# Revit family: PGR_Noken_SntryApplncTrps_Rondo
name_source: partatom
category: Plumbing Fixtures
revit_build: Autodesk Revit 2017 (Build: 20171027_0315(x64)
units: mm (PartAtom-declared; Revit-internal decimal feet)

## family parameters
Always vertical = Yes
Cut with Voids When Loaded = No
Host = Wall
OmniClass Number = 23.45.55.11
OmniClass Title = Sanitary Components
Part Type = Normal
Room Calculation Point = No
Round Connector Dimension = Use Diameter
Shared = Yes

## types (1)
- Rondo-100067431
    AccessibilityPerformance = SeeProductInformation for technical PDF
    ApplicationType = Basin
    AssetType = Fixed
    BIMObjectName = PGR_Noken_SanitaryApplianceTraps_Rondo_Chrome-65x330-380x145-255mm-100067431
    Category = Pr_65_52_25_75: Sanitary appliance traps
    CodePerformance = EN 274
    Collection = Rondo
    Color = Chrome
    Description = Rondo Bottle trap. UK size 35 mm diameter. Material brass, finish chrome plated, nominal length 330-380 mm, nominal width 65 mm, nominal height 145-255 mm, net product weight 0,9 kg . Normative UNE EN 274
    DurationUnit = year
    Features = See ProductInformation for technical PDF
    Finish = Chrome plated
    IfcExportAs = IfcWasteTerminalType
    IfcExportType = WasteTrap
    InletConnectionSize = 40 mm  [stored 0.131234 ft]
    ManufacturerURL = www.noken.com
    Material = Brass
    MaterialMetal = PGR_Noken_Brass_Chrome
    Model = 100067431
    ModelNumber = 100067431
    ModelReference = RONDO BOTTLE TRAP
    NBSDescription = Sanitary appliance traps
    NBSReference = 90-10-60/410
    Name = SanitaryApplianceTraps_Rondo_Chrome-65x330-380x145-255mm-100067431
    NettWeight = 0.9
    NominalHeight = 255 mm  [stored 0.836614 ft]
    NominalHeightRange = 145-255
    NominalLength = 380 mm
    NominalLengthRange = 330-380
    NominalWidth = 65 mm  [stored 0.213255 ft]
    NumberOfConnections = 2
    OutletConnectionSize = 32 mm  [stored 0.104987 ft]
    ProductInformation = http://calidad.info-grupo.com:8081
    Reference = -
    Size = 65x330-380x145-255 mm
    Status = UNSET
    SustainabilityPerformance = See ProductInformation for technical PDF
    TechnicalDrawing = See ProductInformation for technical PDF
    Type Image = 100067431.jpg
    URL = www.noken.com
    Uniclass2015Code = Pr_65_52_25_75
    Uniclass2015Title = Sanitary appliance traps
    Uniclass2015Version = V1_8
    Version = 1
    WFU = 1
    WarrantyDescription = See ProductInformation for technical PDF
    WarrantyDurationUnit = year
    WasteTrapType = UNSET
    WaterInlet = G 1-1/4"

note: [stored X ft] marks values corroborated as IEEE doubles in the binary element streams (Revit-internal decimal feet)

## geometry (parser evidence)
native form markers: Blend x2
no freeform markers — native parametric forms only
